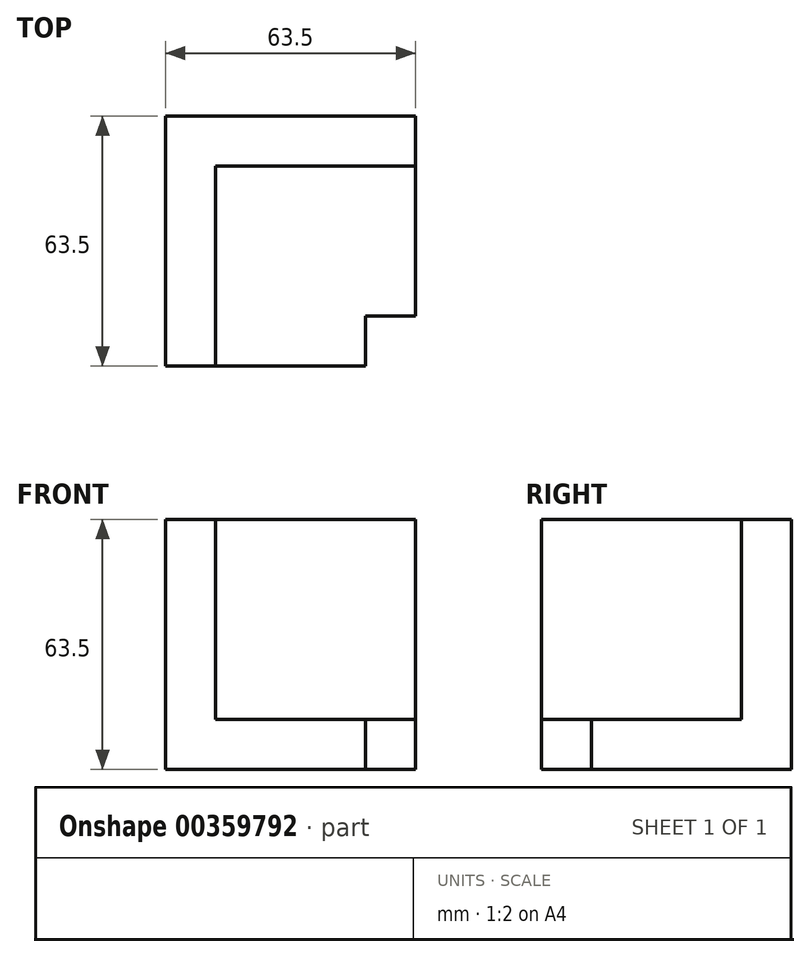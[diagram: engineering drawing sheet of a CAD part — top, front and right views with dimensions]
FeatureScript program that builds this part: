
annotation { "Feature Type Name" : "Feature", "Feature Type Description" : "" }
export const myFeature = defineFeature(function(context is Context, id is Id, definition is map)
    precondition{}
    {
        {
            var Q0;
            Q0=qCreatedBy(makeId("Top.planeOp"),FACE);
            var sketch = newSketch(context, id + "F0", { "sketchPlane" : qUnion([Q0])});
            skLineSegment(sketch, "E0.bottom", {"start": v(0, 0) * mm, "end": v(63.5, 0) * mm});
            skLineSegment(sketch, "E0.top", {"start": v(0, -63.5) * mm, "end": v(63.5, -63.5) * mm});
            skLineSegment(sketch, "E0.left", {"start": v(0, 0) * mm, "end": v(0, -63.5) * mm});
            skLineSegment(sketch, "E0.right", {"start": v(63.5, 0) * mm, "end": v(63.5, -63.5) * mm});
            skSolve(sketch);
        }
        {
            var Q0;
            Q0=makeQuery(id+"F0.imprint","IMPRINT",FACE,{"disambiguationData":[TD([[makeQuery(id+"F0.imprint","IMPRINT",EDGE,{"derivedFrom":sQuery(id+"F0.wireOp",EDGE,"E0.bottom")}),-1.0]])]});
            extrude(context, id + "F1", {"entities" : qUnion([Q0]), "depth" : 12.7 * mm});
        }
        {
            var Q0;
            Q0=makeQuery(id+"F1.opExtrude","CAP_FACE",FACE,{"disambiguationData":[OSD([sQuery(id+"F0.wireOp",EDGE,"E0.bottom"),sQuery(id+"F0.wireOp",EDGE,"E0.top"),sQuery(id+"F0.wireOp",EDGE,"E0.left"),sQuery(id+"F0.wireOp",EDGE,"E0.right")])],"isStart":false});
            var sketch = newSketch(context, id + "F2", { "sketchPlane" : qUnion([Q0])});
            skLineSegment(sketch, "E1.bottom", {"start": v(0, 0) * mm, "end": v(63.5, 0) * mm});
            skLineSegment(sketch, "E1.top", {"start": v(0, -12.7) * mm, "end": v(63.5, -12.7) * mm});
            skLineSegment(sketch, "E1.left", {"start": v(0, 0) * mm, "end": v(0, -12.7) * mm});
            skLineSegment(sketch, "E1.right", {"start": v(63.5, 0) * mm, "end": v(63.5, -12.7) * mm});
            skSolve(sketch);
        }
        {
            var Q0;
            Q0=makeQuery(id+"F2.imprint","IMPRINT",FACE,{"disambiguationData":[TD([[makeQuery(id+"F2.imprint","IMPRINT",EDGE,{"derivedFrom":sQuery(id+"F2.wireOp",EDGE,"E1.bottom")}),-1.0]])]});
            extrude(context, id + "F3", {"entities" : qUnion([Q0]), "operationType" : NewBodyOperationType.ADD, "depth" : 50.8 * mm});
        }
        {
            var Q0;
            Q0=makeQuery(id+"F1.opExtrude","CAP_FACE",FACE,{"disambiguationData":[OSD([sQuery(id+"F0.wireOp",EDGE,"E0.bottom"),sQuery(id+"F0.wireOp",EDGE,"E0.top"),sQuery(id+"F0.wireOp",EDGE,"E0.left"),sQuery(id+"F0.wireOp",EDGE,"E0.right")])],"isStart":false});
            var sketch = newSketch(context, id + "F4", { "sketchPlane" : qUnion([Q0])});
            skLineSegment(sketch, "E2.bottom", {"start": v(0, -12.7) * mm, "end": v(12.7, -12.7) * mm});
            skLineSegment(sketch, "E2.top", {"start": v(0, -63.5) * mm, "end": v(12.7, -63.5) * mm});
            skLineSegment(sketch, "E2.left", {"start": v(0, -12.7) * mm, "end": v(0, -63.5) * mm});
            skLineSegment(sketch, "E2.right", {"start": v(12.7, -12.7) * mm, "end": v(12.7, -63.5) * mm});
            skSolve(sketch);
        }
        {
            var Q0;
            Q0=makeQuery(id+"F4.imprint","IMPRINT",FACE,{"disambiguationData":[TD([[makeQuery(id+"F4.imprint","IMPRINT",EDGE,{"derivedFrom":sQuery(id+"F4.wireOp",EDGE,"E2.bottom")}),-1.0]])]});
            extrude(context, id + "F5", {"entities" : qUnion([Q0]), "operationType" : NewBodyOperationType.ADD, "depth" : 50.8 * mm});
        }
        {
            var Q0;
            Q0=makeQuery(id+"F1.opExtrude","CAP_FACE",FACE,{"disambiguationData":[OSD([sQuery(id+"F0.wireOp",EDGE,"E0.bottom"),sQuery(id+"F0.wireOp",EDGE,"E0.top"),sQuery(id+"F0.wireOp",EDGE,"E0.left"),sQuery(id+"F0.wireOp",EDGE,"E0.right")])],"isStart":false});
            var sketch = newSketch(context, id + "F6", { "sketchPlane" : qUnion([Q0])});
            skLineSegment(sketch, "E3.bottom", {"start": v(50.8, -63.5) * mm, "end": v(63.5, -63.5) * mm});
            skLineSegment(sketch, "E3.top", {"start": v(50.8, -50.8) * mm, "end": v(63.5, -50.8) * mm});
            skLineSegment(sketch, "E3.left", {"start": v(50.8, -63.5) * mm, "end": v(50.8, -50.8) * mm});
            skLineSegment(sketch, "E3.right", {"start": v(63.5, -63.5) * mm, "end": v(63.5, -50.8) * mm});
            skSolve(sketch);
        }
        {
            var Q0;
            Q0=makeQuery(id+"F6.imprint","IMPRINT",FACE,{"disambiguationData":[TD([[makeQuery(id+"F6.imprint","IMPRINT",EDGE,{"derivedFrom":sQuery(id+"F6.wireOp",EDGE,"E3.bottom")}),1.0]])]});
            extrude(context, id + "F7", {"entities" : qUnion([Q0]), "operationType" : NewBodyOperationType.REMOVE, "oppositeDirection" : true, "depth" : 25.4 * mm});
        }
    });
